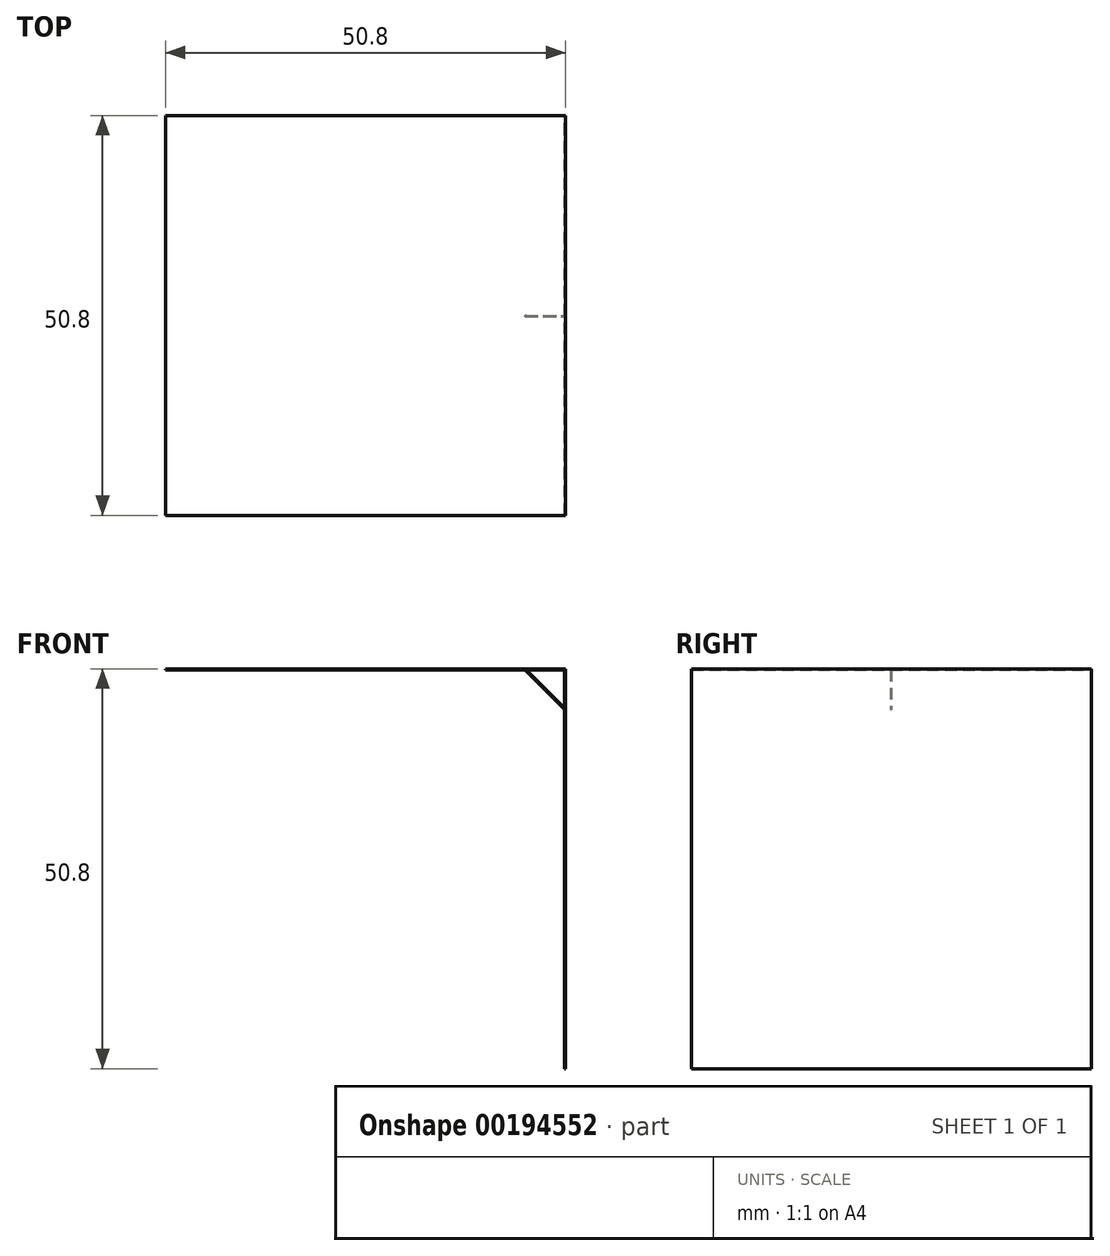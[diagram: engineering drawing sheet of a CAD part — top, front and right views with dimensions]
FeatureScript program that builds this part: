
annotation { "Feature Type Name" : "Feature", "Feature Type Description" : "" }
export const myFeature = defineFeature(function(context is Context, id is Id, definition is map)
    precondition{}
    {
        {
            var Q0;
            Q0=qCreatedBy(makeId("Front.planeOp"),FACE);
            var sketch = newSketch(context, id + "F0", { "sketchPlane" : qUnion([Q0])});
            skLineSegment(sketch, "E0", {"start": v(0, 0) * mm, "end": v(0, 50.8) * mm});
            skLineSegment(sketch, "E1", {"start": v(-50.8, 50.8) * mm, "end": v(0, 50.8) * mm});
            skLineSegment(sketch, "E2", {"start": v(-50.8, 50.8) * mm, "end": v(-50.8, 50.67) * mm});
            skLineSegment(sketch, "E3", {"start": v(-0.13, 50.67) * mm, "end": v(-50.8, 50.67) * mm});
            skLineSegment(sketch, "E4", {"start": v(-0.13, 50.67) * mm, "end": v(-0.13, 0) * mm});
            skLineSegment(sketch, "E5", {"start": v(0, 0) * mm, "end": v(-0.13, 0) * mm});
            skSolve(sketch);
        }
        {
            var Q0;
            Q0 = qSketchRegion(id + "F0", true);
            extrude(context, id + "F1", {"entities" : qUnion([Q0]), "depth" : 25.4 * mm});
        }
        {
            var Q0;
            Q0=makeQuery(id+"F1.opExtrude","CAP_FACE",FACE,{"disambiguationData":[OSD([sQuery(id+"F0.wireOp",EDGE,"E0"),sQuery(id+"F0.wireOp",EDGE,"E1"),sQuery(id+"F0.wireOp",EDGE,"E2"),sQuery(id+"F0.wireOp",EDGE,"E3"),sQuery(id+"F0.wireOp",EDGE,"E4"),sQuery(id+"F0.wireOp",EDGE,"E5")])],"isStart":false});
            var sketch = newSketch(context, id + "F2", { "sketchPlane" : qUnion([Q0])});
            skLineSegment(sketch, "E6", {"start": v(-5.16, 50.67) * mm, "end": v(-0.13, 45.64) * mm});
            skLineSegment(sketch, "E7", {"start": v(-5.16, 50.67) * mm, "end": v(-4.98, 50.67) * mm});
            skLineSegment(sketch, "E8", {"start": v(-4.98, 50.67) * mm, "end": v(-0.13, 45.82) * mm});
            skLineSegment(sketch, "E9", {"start": v(-0.13, 45.82) * mm, "end": v(-0.13, 45.64) * mm});
            skSolve(sketch);
        }
        {
            var Q0;
            Q0 = qSketchRegion(id + "F2", true);
            extrude(context, id + "F3", {"entities" : qUnion([Q0]), "depth" : 0.13 * mm});
        }
        {
            var Q0;
            Q0 = qSketchRegion(id + "F0", true);
            extrude(context, id + "F4", {"entities" : qUnion([Q0]), "operationType" : NewBodyOperationType.ADD, "depth" : 50.8 * mm});
        }
    });
